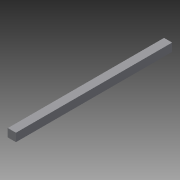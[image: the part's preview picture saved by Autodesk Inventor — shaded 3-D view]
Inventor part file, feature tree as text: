
AUTODESK INVENTOR PART (.ipt)
format: ipt  version: 2013 (Build 170138000, 138)  size: 67,072 bytes
history: native  units: in
note: dims shown in document units (in); Inventor stores cm internally (conversion verified against a paired STEP export)
features: extrude x1, sketch x1
ambient origin geometry x8: Origin, YZ Plane, XZ Plane, XY Plane, X Axis, Y Axis, Z Axis, Center Point
bodies: Solid1 (feature_tree)
feature tree (2):
  extrude  "Extrusion1"  Depth=0.125in
  sketch  "Sketch1"  dims[d0=25.5in d1=0.125in d2=0.125in d3=2.4031in d4=0.0in]
